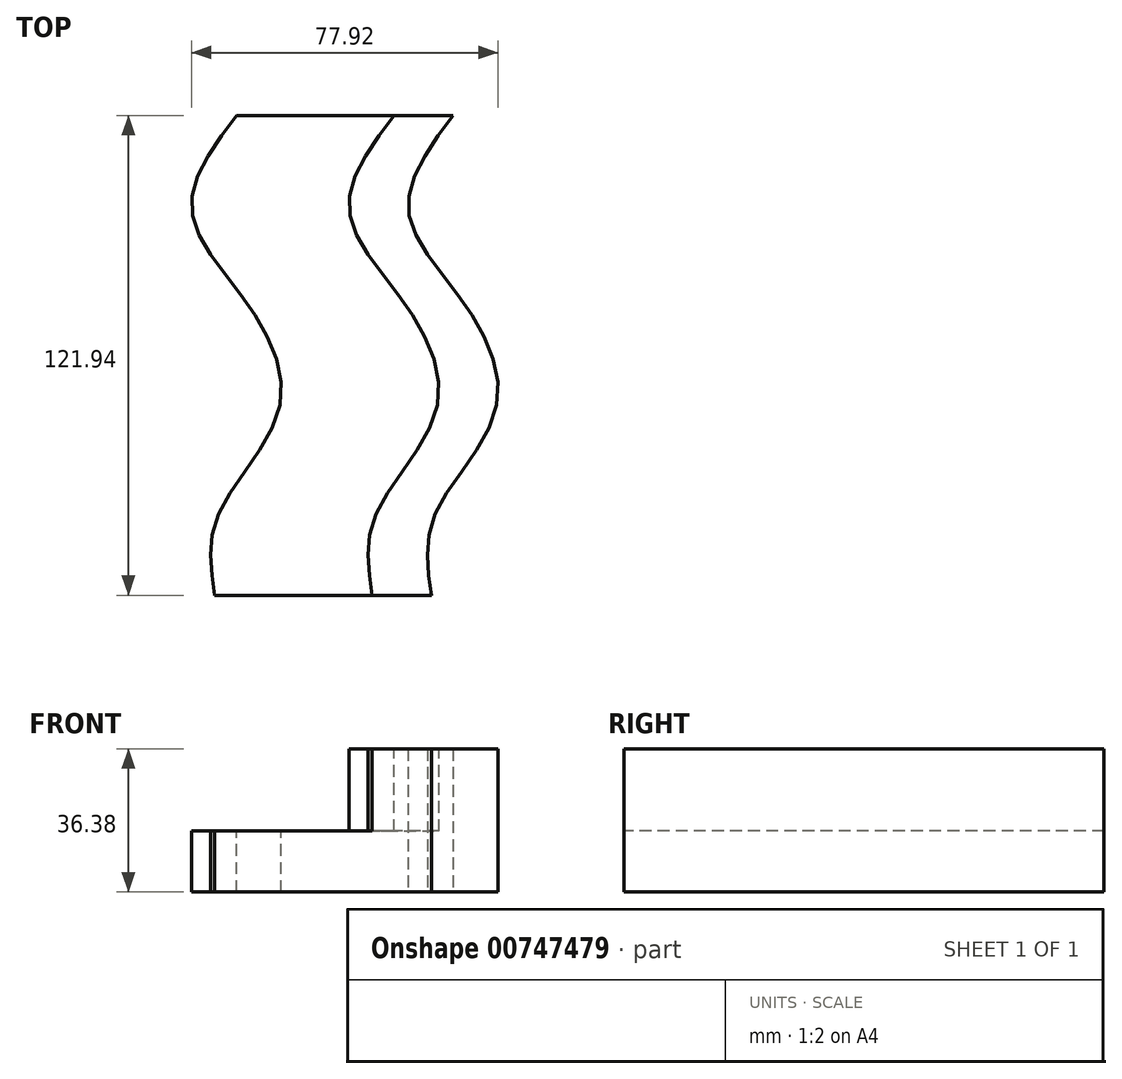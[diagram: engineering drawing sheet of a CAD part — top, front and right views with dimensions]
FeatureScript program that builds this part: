
annotation { "Feature Type Name" : "Feature", "Feature Type Description" : "" }
export const myFeature = defineFeature(function(context is Context, id is Id, definition is map)
    precondition{}
    {
        {
            var Q0;
            Q0=qCreatedBy(makeId("Top.planeOp"),FACE);
            var sketch = newSketch(context, id + "F0", { "sketchPlane" : qUnion([Q0])});
            skFitSpline(sketch, "E0", {"points": [v(-5.88, 58.59) * mm, v(-17.26, 34.6) * mm, v(-2.74, 10.26) * mm, v(4.89, -16.26) * mm, v(-10.58, -43.07) * mm, v(-11.4, -63.35) * mm], "startDerivative": vector(-90.55, -121.6) * mm, "endDerivative": vector(17.72, -114.8) * mm});
            skSolve(sketch);
        }
        {
            var Q0;
            Q0=qCreatedBy(makeId("Front.planeOp"),FACE);
            var sketch = newSketch(context, id + "F1", { "sketchPlane" : qUnion([Q0])});
            skLineSegment(sketch, "E1", {"start": v(0, 0) * mm, "end": v(0, 15.51) * mm});
            skLineSegment(sketch, "E2", {"start": v(0, 15.51) * mm, "end": v(40.01, 15.51) * mm});
            skLineSegment(sketch, "E3", {"start": v(40.01, 15.51) * mm, "end": v(40.01, 36.38) * mm});
            skLineSegment(sketch, "E4", {"start": v(40.01, 36.38) * mm, "end": v(55.07, 36.38) * mm});
            skLineSegment(sketch, "E5", {"start": v(55.07, 36.38) * mm, "end": v(55.07, 0) * mm});
            skLineSegment(sketch, "E6", {"start": v(55.07, 0) * mm, "end": v(0, 0) * mm});
            skSolve(sketch);
        }
        {
            var Q0;
            Q0=makeQuery(id+"F1.imprint","IMPRINT",FACE,{"disambiguationData":[TD([[makeQuery(id+"F1.imprint","IMPRINT",EDGE,{"derivedFrom":sQuery(id+"F1.wireOp",EDGE,"E1")}),-1.0]])]});
            var Q1;
            Q1=sQuery(id+"F0.wireOp",EDGE,"E0");
            sweep(context, id + "F2", {"profiles" : qUnion([Q0]), "path" : qUnion([Q1]), "keepProfileOrientation" : true});
        }
    });
